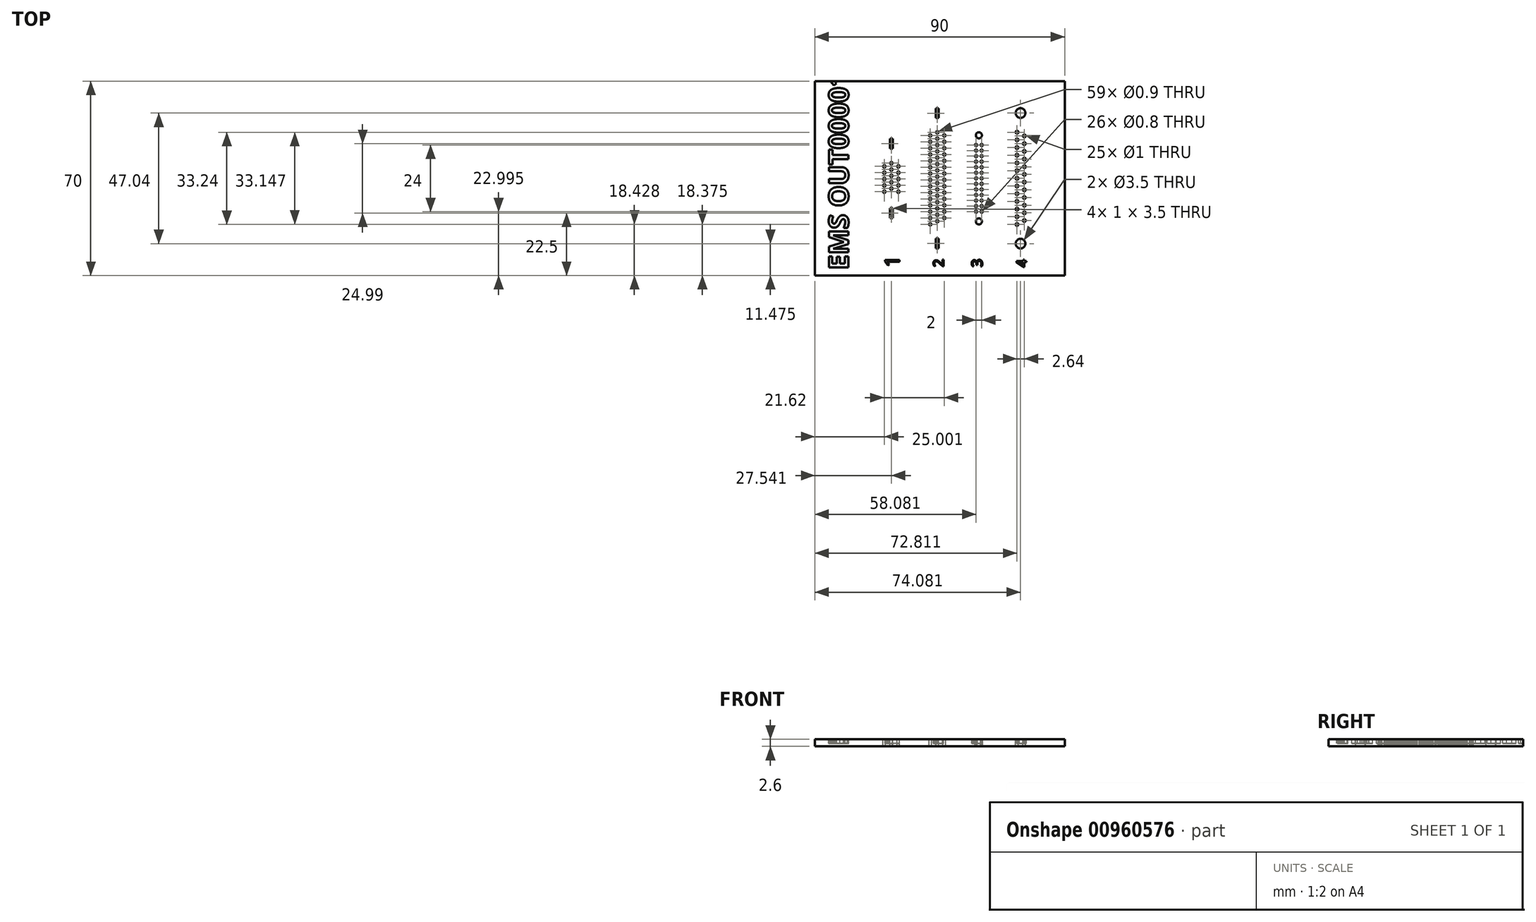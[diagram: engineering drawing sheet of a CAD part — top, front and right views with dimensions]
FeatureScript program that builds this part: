
annotation { "Feature Type Name" : "Feature", "Feature Type Description" : "" }
export const myFeature = defineFeature(function(context is Context, id is Id, definition is map)
    precondition{}
    {
        {
            var Q0;
            Q0=qCreatedBy(makeId("Top.planeOp"),FACE);
            var sketch = newSketch(context, id + "F0", { "sketchPlane" : qUnion([Q0])});
            skLineSegment(sketch, "E0.bottom", {"start": v(-43.16, 48.34) * mm, "end": v(46.84, 48.34) * mm});
            skLineSegment(sketch, "E0.top", {"start": v(-43.16, -21.66) * mm, "end": v(46.84, -21.66) * mm});
            skLineSegment(sketch, "E0.left", {"start": v(-43.16, 48.34) * mm, "end": v(-43.16, -21.66) * mm});
            skLineSegment(sketch, "E0.right", {"start": v(46.84, 48.34) * mm, "end": v(46.84, -21.66) * mm});
            skSolve(sketch);
        }
        {
            var Q0;
            Q0=makeQuery(id+"F0.imprint","IMPRINT",FACE,{"disambiguationData":[TD([[makeQuery(id+"F0.imprint","IMPRINT",EDGE,{"derivedFrom":sQuery(id+"F0.wireOp",EDGE,"E0.bottom")}),-1.0]])]});
            extrude(context, id + "F1", {"entities" : qUnion([Q0]), "depth" : 2.6 * mm, "offsetDistance" : 25 * mm});
        }
        {
            var Q0;
            Q0=makeQuery(id+"F1.opExtrude","CAP_FACE",FACE,{"disambiguationData":[OSD([sQuery(id+"F0.wireOp",EDGE,"E0.bottom"),sQuery(id+"F0.wireOp",EDGE,"E0.top"),sQuery(id+"F0.wireOp",EDGE,"E0.left"),sQuery(id+"F0.wireOp",EDGE,"E0.right")])],"isStart":false});
            var sketch = newSketch(context, id + "F2", { "sketchPlane" : qUnion([Q0])});
            skText(sketch, "E1", { "text": "EMS OUT00001", "fontName": "OpenSans-Bold.ttf"});
            skText(sketch, "E2", { "text": "1", "fontName": "OpenSans-Regular.ttf"});
            skText(sketch, "E3", { "text": "2", "fontName": "OpenSans-Regular.ttf"});
            skText(sketch, "E4", { "text": "3", "fontName": "OpenSans-Regular.ttf"});
            skText(sketch, "E5", { "text": "4", "fontName": "OpenSans-Regular.ttf"});
            const initialGuessF2  = {"E1": [-0.0311, -0.01966, 0, 1, 0.00705], "E2": [-0.0127, -0.01866, 0, 1, 0.00522], "E3": [0.00325, -0.01866, 0, 1, 0.0037], "E4": [0.0171, -0.01866, 0, 1, 0.00374], "E5": [0.03303, -0.01866, 0, 1, 0.0035]};
            skSetInitialGuess(sketch, initialGuessF2);
            skSolve(sketch);
        }
        {
            var Q0;
            Q0=qSketchRegion(id+"F2",true);
            extrude(context, id + "F3", {"entities" : qUnion([Q0]), "operationType" : NewBodyOperationType.REMOVE, "oppositeDirection" : true, "depth" : 1.5 * mm, "offsetDistance" : 25 * mm});
        }
        {
            var Q0;
            {var subQ0=sQuery(id+"F0.wireOp",EDGE,"E0.left");var subQ1=sQuery(id+"F0.wireOp",EDGE,"E0.bottom");var subQ2=sQuery(id+"F0.wireOp",EDGE,"E0.right");var subQ3=sQuery(id+"F0.wireOp",EDGE,"E0.top");Q0=makeQuery(id+"F3.boolean.opBoolean","SPLIT",FACE,{"disambiguationData":[TD([makeQuery(id+"F1.opExtrude","SWEPT_FACE",FACE,{"disambiguationData":[OSD([subQ1])]})])],"derivedFrom":makeQuery(id+"F1.opExtrude","CAP_FACE",FACE,{"disambiguationData":[OSD([subQ1,subQ3,subQ0,subQ2])],"isStart":false})});}
            var sketch = newSketch(context, id + "F4", { "sketchPlane" : qUnion([Q0])});
            skCircle(sketch, "E6", {"center": v(-18.16, 8.51) * mm, "radius": 0.45 * mm});
            skCircle(sketch, "E7", {"center": v(-18.16, 10.8) * mm, "radius": 0.45 * mm});
            skCircle(sketch, "E8", {"center": v(-18.16, 13.09) * mm, "radius": 0.45 * mm});
            skCircle(sketch, "E9", {"center": v(-18.16, 15.37) * mm, "radius": 0.45 * mm});
            skCircle(sketch, "E10", {"center": v(-18.16, 17.66) * mm, "radius": 0.45 * mm});
            skCircle(sketch, "E11", {"center": v(-15.62, 9.66) * mm, "radius": 0.45 * mm});
            skCircle(sketch, "E12", {"center": v(-15.62, 11.94) * mm, "radius": 0.45 * mm});
            skCircle(sketch, "E13", {"center": v(-15.62, 14.23) * mm, "radius": 0.45 * mm});
            skCircle(sketch, "E14", {"center": v(-15.62, 16.51) * mm, "radius": 0.45 * mm});
            skCircle(sketch, "E15", {"center": v(-15.62, 18.8) * mm, "radius": 0.45 * mm});
            skCircle(sketch, "E16", {"center": v(-13.08, 8.51) * mm, "radius": 0.45 * mm});
            skCircle(sketch, "E17", {"center": v(-13.08, 10.8) * mm, "radius": 0.45 * mm});
            skCircle(sketch, "E18", {"center": v(-13.08, 13.09) * mm, "radius": 0.45 * mm});
            skCircle(sketch, "E19", {"center": v(-13.08, 15.37) * mm, "radius": 0.45 * mm});
            skCircle(sketch, "E20", {"center": v(-13.08, 17.66) * mm, "radius": 0.45 * mm});
            skLineSegment(sketch, "E21.bottom", {"start": v(-16.12, 24.08) * mm, "end": v(-15.12, 24.08) * mm});
            skLineSegment(sketch, "E21.top", {"start": v(-16.12, 27.58) * mm, "end": v(-15.12, 27.58) * mm});
            skLineSegment(sketch, "E21.left", {"start": v(-16.12, 24.08) * mm, "end": v(-16.12, 27.58) * mm});
            skLineSegment(sketch, "E21.right", {"start": v(-15.12, 24.08) * mm, "end": v(-15.12, 27.58) * mm});
            skLineSegment(sketch, "E22.bottom", {"start": v(-16.12, -0.9) * mm, "end": v(-15.12, -0.9) * mm});
            skLineSegment(sketch, "E22.top", {"start": v(-16.12, 2.6) * mm, "end": v(-15.12, 2.6) * mm});
            skLineSegment(sketch, "E22.left", {"start": v(-16.12, -0.9) * mm, "end": v(-16.12, 2.6) * mm});
            skLineSegment(sketch, "E22.right", {"start": v(-15.12, -0.9) * mm, "end": v(-15.12, 2.6) * mm});
            skCircle(sketch, "E23", {"center": v(-1.62, 19.63) * mm, "radius": 0.45 * mm});
            skCircle(sketch, "E24", {"center": v(-1.62, 21.91) * mm, "radius": 0.45 * mm});
            skCircle(sketch, "E25", {"center": v(-1.62, 24.2) * mm, "radius": 0.45 * mm});
            skCircle(sketch, "E26", {"center": v(-1.62, 26.49) * mm, "radius": 0.45 * mm});
            skCircle(sketch, "E27", {"center": v(-1.62, 28.77) * mm, "radius": 0.45 * mm});
            skCircle(sketch, "E28", {"center": v(0.92, 20.77) * mm, "radius": 0.45 * mm});
            skCircle(sketch, "E29", {"center": v(0.92, 23.06) * mm, "radius": 0.45 * mm});
            skCircle(sketch, "E30", {"center": v(0.92, 25.34) * mm, "radius": 0.45 * mm});
            skCircle(sketch, "E31", {"center": v(0.92, 27.63) * mm, "radius": 0.45 * mm});
            skCircle(sketch, "E32", {"center": v(0.92, 29.92) * mm, "radius": 0.45 * mm});
            skCircle(sketch, "E33", {"center": v(3.46, 19.63) * mm, "radius": 0.45 * mm});
            skCircle(sketch, "E34", {"center": v(3.46, 21.91) * mm, "radius": 0.45 * mm});
            skCircle(sketch, "E35", {"center": v(3.46, 24.2) * mm, "radius": 0.45 * mm});
            skCircle(sketch, "E36", {"center": v(3.46, 26.49) * mm, "radius": 0.45 * mm});
            skCircle(sketch, "E37", {"center": v(3.46, 28.77) * mm, "radius": 0.45 * mm});
            skLineSegment(sketch, "E38.bottom", {"start": v(0.42, 35.05) * mm, "end": v(1.42, 35.05) * mm});
            skLineSegment(sketch, "E38.top", {"start": v(0.42, 38.55) * mm, "end": v(1.42, 38.55) * mm});
            skLineSegment(sketch, "E38.left", {"start": v(0.42, 35.05) * mm, "end": v(0.42, 38.55) * mm});
            skLineSegment(sketch, "E38.right", {"start": v(1.42, 35.05) * mm, "end": v(1.42, 38.55) * mm});
            skCircle(sketch, "E39", {"center": v(-1.62, 8.2) * mm, "radius": 0.45 * mm});
            skCircle(sketch, "E40", {"center": v(-1.62, 10.48) * mm, "radius": 0.45 * mm});
            skCircle(sketch, "E41", {"center": v(-1.62, 12.77) * mm, "radius": 0.45 * mm});
            skCircle(sketch, "E42", {"center": v(-1.62, 15.06) * mm, "radius": 0.45 * mm});
            skCircle(sketch, "E43", {"center": v(-1.62, 17.34) * mm, "radius": 0.45 * mm});
            skCircle(sketch, "E44", {"center": v(0.92, 9.34) * mm, "radius": 0.45 * mm});
            skCircle(sketch, "E45", {"center": v(0.92, 11.63) * mm, "radius": 0.45 * mm});
            skCircle(sketch, "E46", {"center": v(0.92, 13.91) * mm, "radius": 0.45 * mm});
            skCircle(sketch, "E47", {"center": v(0.92, 16.2) * mm, "radius": 0.45 * mm});
            skCircle(sketch, "E48", {"center": v(0.92, 18.49) * mm, "radius": 0.45 * mm});
            skCircle(sketch, "E49", {"center": v(3.46, 8.2) * mm, "radius": 0.45 * mm});
            skCircle(sketch, "E50", {"center": v(3.46, 10.48) * mm, "radius": 0.45 * mm});
            skCircle(sketch, "E51", {"center": v(3.46, 12.77) * mm, "radius": 0.45 * mm});
            skCircle(sketch, "E52", {"center": v(3.46, 15.06) * mm, "radius": 0.45 * mm});
            skCircle(sketch, "E53", {"center": v(3.46, 17.34) * mm, "radius": 0.45 * mm});
            skCircle(sketch, "E54", {"center": v(-1.62, -3.23) * mm, "radius": 0.45 * mm});
            skCircle(sketch, "E55", {"center": v(-1.62, -0.95) * mm, "radius": 0.45 * mm});
            skCircle(sketch, "E56", {"center": v(-1.62, 1.34) * mm, "radius": 0.45 * mm});
            skCircle(sketch, "E57", {"center": v(-1.62, 3.63) * mm, "radius": 0.45 * mm});
            skCircle(sketch, "E58", {"center": v(-1.62, 5.91) * mm, "radius": 0.45 * mm});
            skCircle(sketch, "E59", {"center": v(0.92, -2.09) * mm, "radius": 0.45 * mm});
            skCircle(sketch, "E60", {"center": v(0.92, 0.2) * mm, "radius": 0.45 * mm});
            skCircle(sketch, "E61", {"center": v(0.92, 2.48) * mm, "radius": 0.45 * mm});
            skCircle(sketch, "E62", {"center": v(0.92, 4.77) * mm, "radius": 0.45 * mm});
            skCircle(sketch, "E63", {"center": v(0.92, 7.06) * mm, "radius": 0.45 * mm});
            skCircle(sketch, "E64", {"center": v(3.46, -0.95) * mm, "radius": 0.45 * mm});
            skCircle(sketch, "E65", {"center": v(3.46, 1.34) * mm, "radius": 0.45 * mm});
            skCircle(sketch, "E66", {"center": v(3.46, 3.63) * mm, "radius": 0.45 * mm});
            skCircle(sketch, "E67", {"center": v(3.46, 5.91) * mm, "radius": 0.45 * mm});
            skLineSegment(sketch, "E68.bottom", {"start": v(0.42, -11.86) * mm, "end": v(1.42, -11.86) * mm});
            skLineSegment(sketch, "E68.top", {"start": v(0.42, -8.36) * mm, "end": v(1.42, -8.36) * mm});
            skLineSegment(sketch, "E68.left", {"start": v(0.42, -11.86) * mm, "end": v(0.42, -8.36) * mm});
            skLineSegment(sketch, "E68.right", {"start": v(1.42, -11.86) * mm, "end": v(1.42, -8.36) * mm});
            skCircle(sketch, "E69", {"center": v(15.92, -2.16) * mm, "radius": 1.1 * mm});
            skCircle(sketch, "E70", {"center": v(15.92, 28.84) * mm, "radius": 1.1 * mm});
            skCircle(sketch, "E71", {"center": v(14.92, 1.34) * mm, "radius": 0.4 * mm});
            skCircle(sketch, "E72", {"center": v(16.92, 1.34) * mm, "radius": 0.4 * mm});
            skCircle(sketch, "E73", {"center": v(14.92, 3.34) * mm, "radius": 0.4 * mm});
            skCircle(sketch, "E74", {"center": v(14.92, 5.34) * mm, "radius": 0.4 * mm});
            skCircle(sketch, "E75", {"center": v(14.92, 7.34) * mm, "radius": 0.4 * mm});
            skCircle(sketch, "E76", {"center": v(14.92, 9.34) * mm, "radius": 0.4 * mm});
            skCircle(sketch, "E77", {"center": v(14.92, 11.34) * mm, "radius": 0.4 * mm});
            skCircle(sketch, "E78", {"center": v(14.92, 13.34) * mm, "radius": 0.4 * mm});
            skCircle(sketch, "E79", {"center": v(14.92, 15.34) * mm, "radius": 0.4 * mm});
            skCircle(sketch, "E80", {"center": v(14.92, 17.34) * mm, "radius": 0.4 * mm});
            skCircle(sketch, "E81", {"center": v(14.92, 19.34) * mm, "radius": 0.4 * mm});
            skCircle(sketch, "E82", {"center": v(14.92, 21.34) * mm, "radius": 0.4 * mm});
            skCircle(sketch, "E83", {"center": v(14.92, 23.34) * mm, "radius": 0.4 * mm});
            skCircle(sketch, "E84", {"center": v(16.92, 3.34) * mm, "radius": 0.4 * mm});
            skCircle(sketch, "E85", {"center": v(16.92, 5.34) * mm, "radius": 0.4 * mm});
            skCircle(sketch, "E86", {"center": v(16.92, 7.34) * mm, "radius": 0.4 * mm});
            skCircle(sketch, "E87", {"center": v(16.92, 9.34) * mm, "radius": 0.4 * mm});
            skCircle(sketch, "E88", {"center": v(16.92, 11.34) * mm, "radius": 0.4 * mm});
            skCircle(sketch, "E89", {"center": v(16.92, 13.34) * mm, "radius": 0.4 * mm});
            skCircle(sketch, "E90", {"center": v(16.92, 15.34) * mm, "radius": 0.4 * mm});
            skCircle(sketch, "E91", {"center": v(16.92, 17.34) * mm, "radius": 0.4 * mm});
            skCircle(sketch, "E92", {"center": v(16.92, 19.34) * mm, "radius": 0.4 * mm});
            skCircle(sketch, "E93", {"center": v(16.92, 21.34) * mm, "radius": 0.4 * mm});
            skCircle(sketch, "E94", {"center": v(16.92, 23.34) * mm, "radius": 0.4 * mm});
            skCircle(sketch, "E95", {"center": v(16.92, 25.34) * mm, "radius": 0.4 * mm});
            skCircle(sketch, "E96", {"center": v(14.92, 25.34) * mm, "radius": 0.4 * mm});
            skCircle(sketch, "E97", {"center": v(30.92, -10.18) * mm, "radius": 1.75 * mm});
            skCircle(sketch, "E98", {"center": v(29.65, -3.28) * mm, "radius": 0.5 * mm});
            skCircle(sketch, "E99", {"center": v(29.65, -0.51) * mm, "radius": 0.5 * mm});
            skCircle(sketch, "E100", {"center": v(29.65, 2.26) * mm, "radius": 0.5 * mm});
            skCircle(sketch, "E101", {"center": v(29.65, 5.03) * mm, "radius": 0.5 * mm});
            skCircle(sketch, "E102", {"center": v(29.65, 7.8) * mm, "radius": 0.5 * mm});
            skCircle(sketch, "E103", {"center": v(29.65, 10.57) * mm, "radius": 0.5 * mm});
            skCircle(sketch, "E104", {"center": v(29.65, 13.34) * mm, "radius": 0.5 * mm});
            skCircle(sketch, "E105", {"center": v(29.65, 16.1) * mm, "radius": 0.5 * mm});
            skCircle(sketch, "E106", {"center": v(29.65, 18.88) * mm, "radius": 0.5 * mm});
            skCircle(sketch, "E107", {"center": v(29.65, 21.65) * mm, "radius": 0.5 * mm});
            skCircle(sketch, "E108", {"center": v(29.65, 24.42) * mm, "radius": 0.5 * mm});
            skCircle(sketch, "E109", {"center": v(29.65, 27.19) * mm, "radius": 0.5 * mm});
            skCircle(sketch, "E110", {"center": v(32.3, -1.88) * mm, "radius": 0.5 * mm});
            skCircle(sketch, "E111", {"center": v(32.3, 0.89) * mm, "radius": 0.5 * mm});
            skCircle(sketch, "E112", {"center": v(32.3, 3.66) * mm, "radius": 0.5 * mm});
            skCircle(sketch, "E113", {"center": v(32.3, 6.43) * mm, "radius": 0.5 * mm});
            skCircle(sketch, "E114", {"center": v(32.3, 9.2) * mm, "radius": 0.5 * mm});
            skCircle(sketch, "E115", {"center": v(32.3, 11.97) * mm, "radius": 0.5 * mm});
            skCircle(sketch, "E116", {"center": v(32.3, 14.74) * mm, "radius": 0.5 * mm});
            skCircle(sketch, "E117", {"center": v(32.3, 17.5) * mm, "radius": 0.5 * mm});
            skCircle(sketch, "E118", {"center": v(32.3, 20.28) * mm, "radius": 0.5 * mm});
            skCircle(sketch, "E119", {"center": v(32.3, 23.05) * mm, "radius": 0.5 * mm});
            skCircle(sketch, "E120", {"center": v(32.3, 25.82) * mm, "radius": 0.5 * mm});
            skCircle(sketch, "E121", {"center": v(32.3, 28.59) * mm, "radius": 0.5 * mm});
            skCircle(sketch, "E122", {"center": v(29.65, 29.96) * mm, "radius": 0.5 * mm});
            skCircle(sketch, "E123", {"center": v(30.92, 36.86) * mm, "radius": 1.75 * mm});
            skSolve(sketch);
        }
        {
            var Q0;
            Q0 = qSketchRegion(id + "F4", true);
            extrude(context, id + "F5", {"entities" : qUnion([Q0]), "operationType" : NewBodyOperationType.REMOVE, "endBound" : BoundingType.UP_TO_NEXT, "oppositeDirection" : true, "depth" : 25 * mm, "offsetDistance" : 25 * mm});
        }
    });
